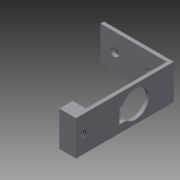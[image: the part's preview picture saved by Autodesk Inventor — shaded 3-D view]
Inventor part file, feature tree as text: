
AUTODESK INVENTOR PART (.ipt)
format: ipt  version: 2015 (Build 190159000, 159)  size: 138,752 bytes
history: native  units: in
note: dims shown in document units (in); Inventor stores cm internally (conversion verified against a paired STEP export)
features: sketch x5, extrude x4, hole x1, projected_geometry x1
ambient origin geometry x8: Origin, YZ Plane, XZ Plane, XY Plane, X Axis, Y Axis, Z Axis, Center Point
bodies: Solid1 (feature_tree)
feature tree (11):
  extrude  "Extrusion1"  Depth=1.0in
  extrude  "Extrusion2"  Depth=0.125in
  extrude  "Extrusion3"  Depth=0.25in
  extrude  "Extrusion4"  Depth=0.05in TaperAngle=0.0deg
  hole  "Hole1"  [1 undecoded]
  sketch  "Sketch1"  dims[d0=0.5in d1=1.0in]
  sketch  "Sketch2"  dims[d2=0.125in d3=0.125in]
  sketch  "Sketch3"  dims[d4=0.25in d5=0.2in]
  sketch  "Sketch4"  dims[d6=0.5in d7=0.05in d8=0.0in]
  sketch  "Sketch5"  dims[d9=0.05in d10=1.35in d11=0.0in d19=1.0in d20=0.0in d21=0.386in d22=0.5in d23=0.25in d24=0.14in d25=0.096in d26=0.08in d27=0.037in d28=0.14in d29=0.66in d30=0.19in d31=0.0in d33=0.19in d35=0.5in d38=0.25in d39=0.098in d40=0.25in d41=0.375in d42=0.25in d43=0.5635in d44=0.375in d45=0.8108in d46=0.092in]
  projected_geometry  "Projected Loop1"
note: 1 required parameter value undecoded (feature->parameter linkage not recoverable at this tier; creation-order binding heuristic only, values carry confidence <= 0.55)
